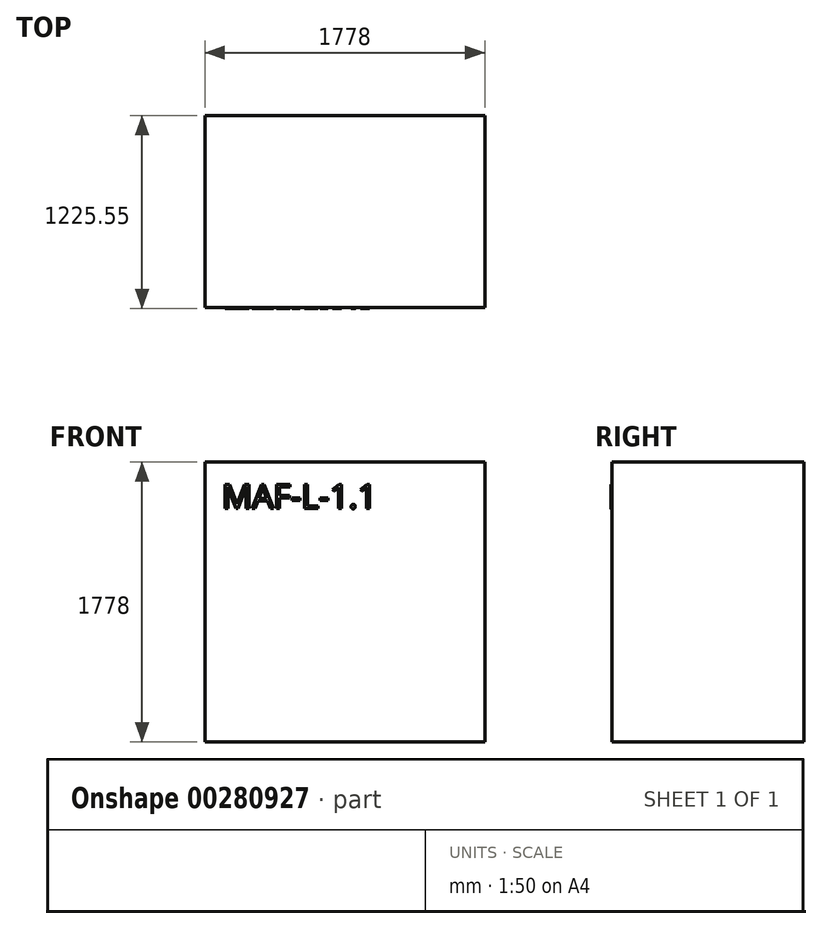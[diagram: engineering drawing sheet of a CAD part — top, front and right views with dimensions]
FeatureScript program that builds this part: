
annotation { "Feature Type Name" : "Feature", "Feature Type Description" : "" }
export const myFeature = defineFeature(function(context is Context, id is Id, definition is map)
    precondition{}
    {
        {
            var Q0;
            Q0=qCreatedBy(makeId("Top.planeOp"),FACE);
            var sketch = newSketch(context, id + "F0", { "sketchPlane" : qUnion([Q0])});
            skLineSegment(sketch, "E0.bottom", {"start": v(0, 0) * mm, "end": v(1778, 0) * mm});
            skLineSegment(sketch, "E0.top", {"start": v(0, 965.2) * mm, "end": v(1778, 965.2) * mm});
            skLineSegment(sketch, "E0.left", {"start": v(0, 0) * mm, "end": v(0, 965.2) * mm});
            skLineSegment(sketch, "E0.right", {"start": v(1778, 0) * mm, "end": v(1778, 965.2) * mm});
            skSolve(sketch);
        }
        {
            var Q0;
            Q0=makeQuery(id+"F0.imprint","IMPRINT",FACE,{"disambiguationData":[TD([[makeQuery(id+"F0.imprint","IMPRINT",EDGE,{"derivedFrom":sQuery(id+"F0.wireOp",EDGE,"E0.bottom")}),1.0]])]});
            extrude(context, id + "F1", {"entities" : qUnion([Q0]), "depth" : 1778 * mm});
        }
        {
            var Q0;
            Q0=makeQuery(id+"F1.opExtrude","SWEPT_FACE",FACE,{"disambiguationData":[OSD([sQuery(id+"F0.wireOp",EDGE,"E0.bottom")])]});
            var sketch = newSketch(context, id + "F2", { "sketchPlane" : qUnion([Q0])});
            skText(sketch, "E1", { "text": "MAF-L-1.1", "fontName": "OpenSans-Regular.ttf"});
            const initialGuessF2  = {"E1": [0.10835, 1.48366, 1, 0, 0.1531]};
            skSetInitialGuess(sketch, initialGuessF2);
            skSolve(sketch);
        }
        {
            var Q0;
            Q0 = qSketchRegion(id + "F2", true);
            extrude(context, id + "F3", {"entities" : qUnion([Q0]), "operationType" : NewBodyOperationType.ADD, "depth" : 6.35 * mm});
        }
        {
            var Q0;
            Q0=makeQuery(id+"F1.opExtrude","SWEPT_FACE",FACE,{"disambiguationData":[OSD([sQuery(id+"F0.wireOp",EDGE,"E0.top")])]});
            extrude(context, id + "F4", {"entities" : qUnion([Q0]), "operationType" : NewBodyOperationType.ADD, "depth" : 254 * mm});
        }
    });
